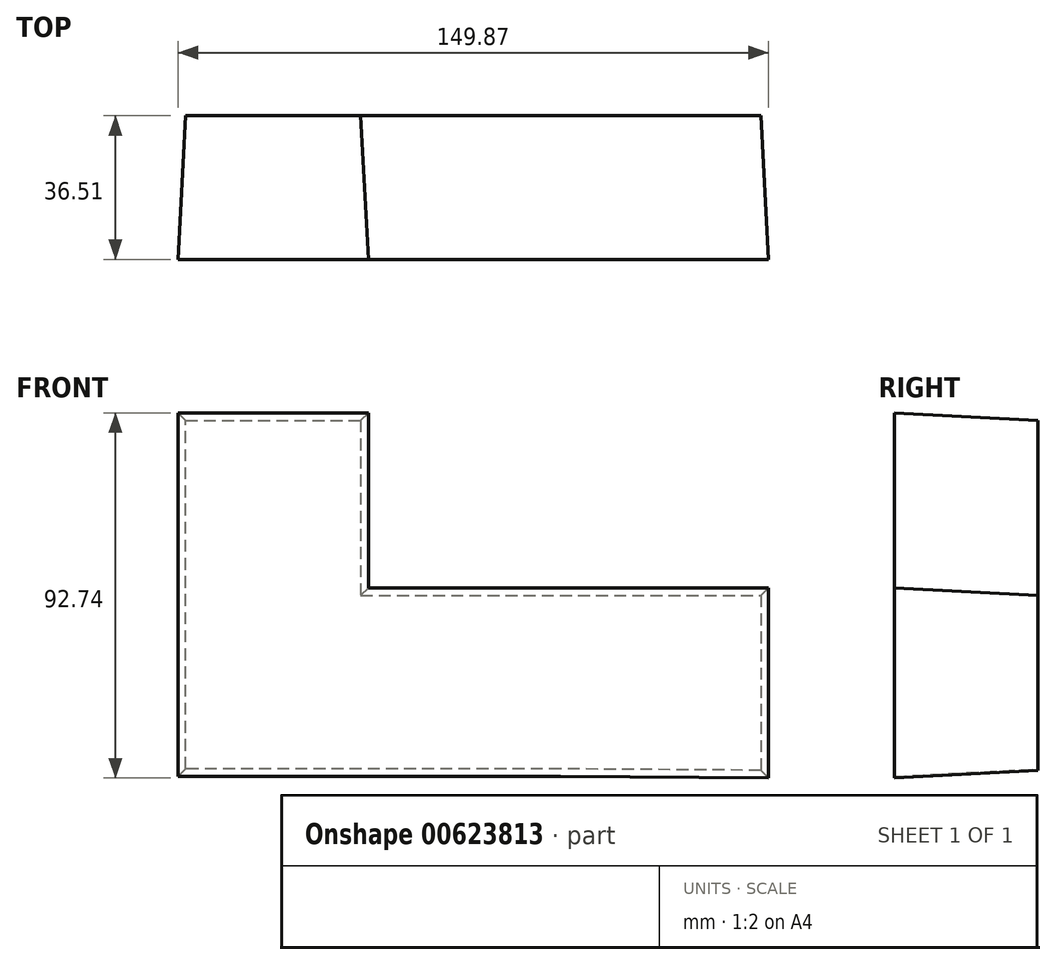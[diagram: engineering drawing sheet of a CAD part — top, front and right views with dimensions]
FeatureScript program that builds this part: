
annotation { "Feature Type Name" : "Feature", "Feature Type Description" : "" }
export const myFeature = defineFeature(function(context is Context, id is Id, definition is map)
    precondition{}
    {
        {
            var Q0;
            Q0=qCreatedBy(makeId("Front.planeOp"),FACE);
            var sketch = newSketch(context, id + "F0", { "sketchPlane" : qUnion([Q0])});
            skLineSegment(sketch, "E0", {"start": v(-105.48, 29.69) * mm, "end": v(-61.03, 29.69) * mm});
            skLineSegment(sketch, "E1", {"start": v(-61.03, 29.69) * mm, "end": v(-61.03, -14.76) * mm});
            skLineSegment(sketch, "E2", {"start": v(-61.03, -14.76) * mm, "end": v(40.57, -14.76) * mm});
            skLineSegment(sketch, "E3", {"start": v(40.57, -14.76) * mm, "end": v(40.57, -59.21) * mm});
            skLineSegment(sketch, "E4", {"start": v(-105.48, 29.69) * mm, "end": v(-105.48, -58.86) * mm});
            skLineSegment(sketch, "E5", {"start": v(-105.48, -58.86) * mm, "end": v(-10.23, -58.86) * mm});
            skLineSegment(sketch, "E6", {"start": v(-10.23, -58.86) * mm, "end": v(40.57, -59.21) * mm});
            skSolve(sketch);
        }
        {
            var Q0;
            Q0=makeQuery(id+"F0.imprint","IMPRINT",FACE,{"disambiguationData":[TD([[makeQuery(id+"F0.imprint","IMPRINT",EDGE,{"derivedFrom":sQuery(id+"F0.wireOp",EDGE,"E0")}),-1.0]])]});
            extrude(context, id + "F1", {"entities" : qUnion([Q0]), "depth" : 36.5 * mm, "offsetDistance" : 25.4 * mm, "hasDraft" : true, "draftAngle" : 3 * degree});
        }
    });
